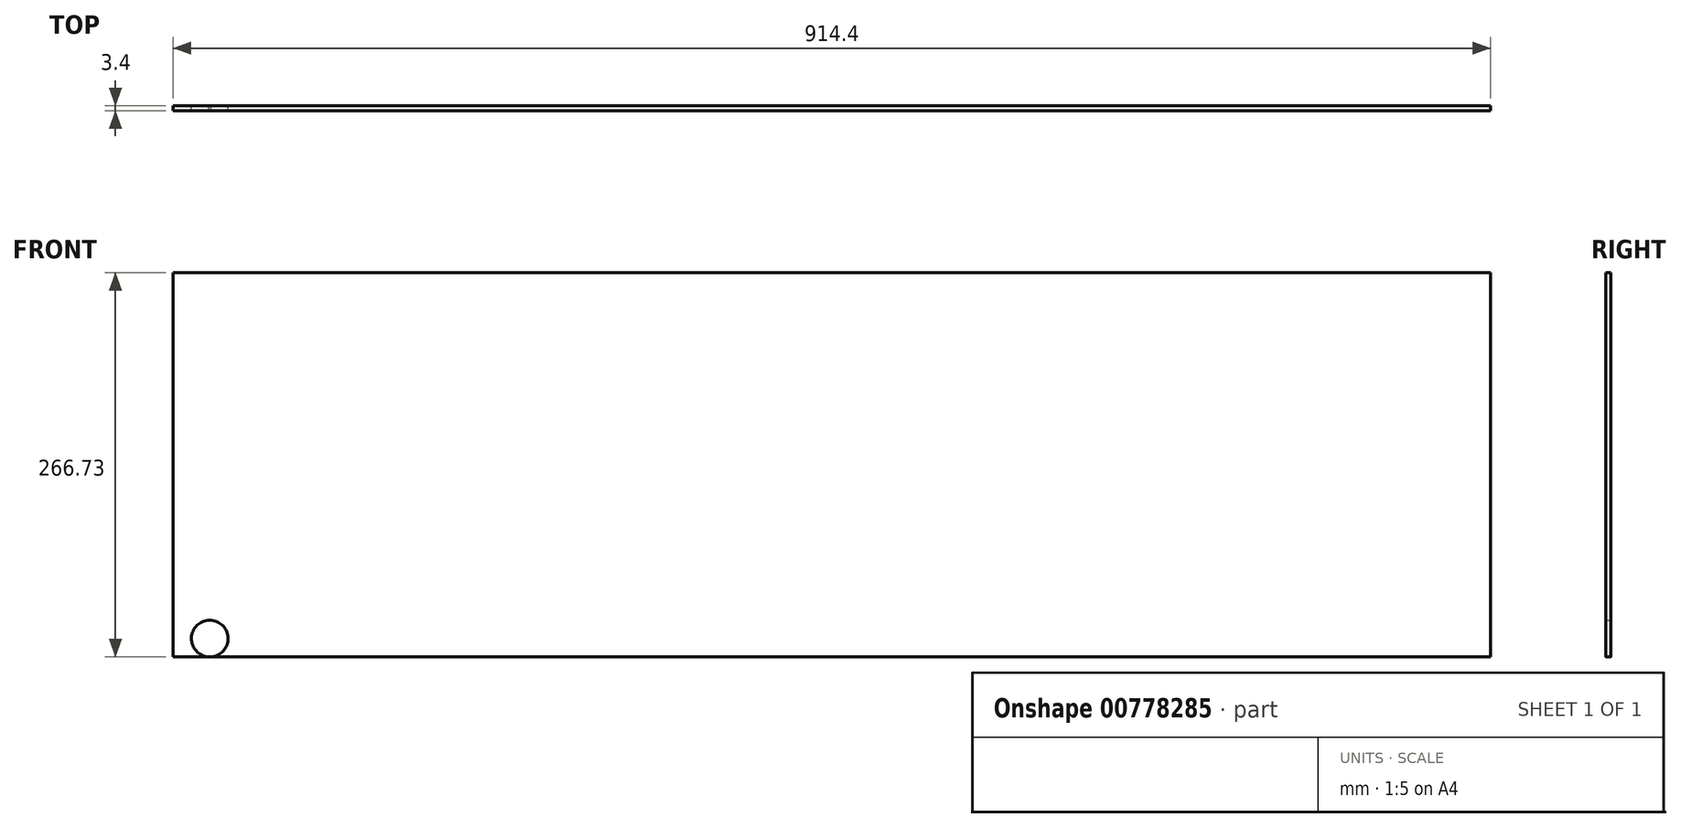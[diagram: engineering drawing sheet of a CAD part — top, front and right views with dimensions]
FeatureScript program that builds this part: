
annotation { "Feature Type Name" : "Feature", "Feature Type Description" : "" }
export const myFeature = defineFeature(function(context is Context, id is Id, definition is map)
    precondition{}
    {
        {
            var Q0;
            Q0=qCreatedBy(makeId("Front.planeOp"),FACE);
            var sketch = newSketch(context, id + "F0", { "sketchPlane" : qUnion([Q0])});
            skLineSegment(sketch, "E0.bottom", {"start": v(-457.2, 133.35) * mm, "end": v(457.2, 133.35) * mm});
            skLineSegment(sketch, "E0.top", {"start": v(-457.2, -133.35) * mm, "end": v(457.2, -133.35) * mm});
            skLineSegment(sketch, "E0.left", {"start": v(-457.2, 133.35) * mm, "end": v(-457.2, -133.35) * mm});
            skLineSegment(sketch, "E0.right", {"start": v(457.2, 133.35) * mm, "end": v(457.2, -133.35) * mm});
            skPoint(sketch, "E0.middle", {"position": v(0, 0) * mm});
            skCircle(sketch, "E1", {"center": v(-431.8, -120.68) * mm, "radius": 12.7 * mm});
            skSolve(sketch);
        }
        {
            var Q0;
            {var subQ0=sQuery(id+"F0.wireOp",EDGE,"E1");var subQ1=sQuery(id+"F0.wireOp",EDGE,"E0.top");var subQ2=makeQuery(id+"F0.imprint","INTERSECT",VERTEX,{"disambiguationData":[OD(0.0)],"derivedFrom":[subQ1,subQ0]});Q0=makeQuery(id+"F0.imprint","IMPRINT",FACE,{"disambiguationData":[TD([[makeQuery(id+"F0.imprint","IMPRINT",EDGE,{"disambiguationData":[TD([[subQ2,-1.0]])],"derivedFrom":subQ1}),-1.0]])]});}
            var Q1;
            Q1=makeQuery(id+"F0.imprint","IMPRINT",FACE,{"disambiguationData":[TD([[makeQuery(id+"F0.imprint","IMPRINT",EDGE,{"derivedFrom":sQuery(id+"F0.wireOp",EDGE,"E0.bottom")}),-1.0]])]});
            extrude(context, id + "F1", {"entities" : qUnion([Q0, Q1]), "depth" : 3.4 * mm, "offsetDistance" : 25.4 * mm});
        }
    });
